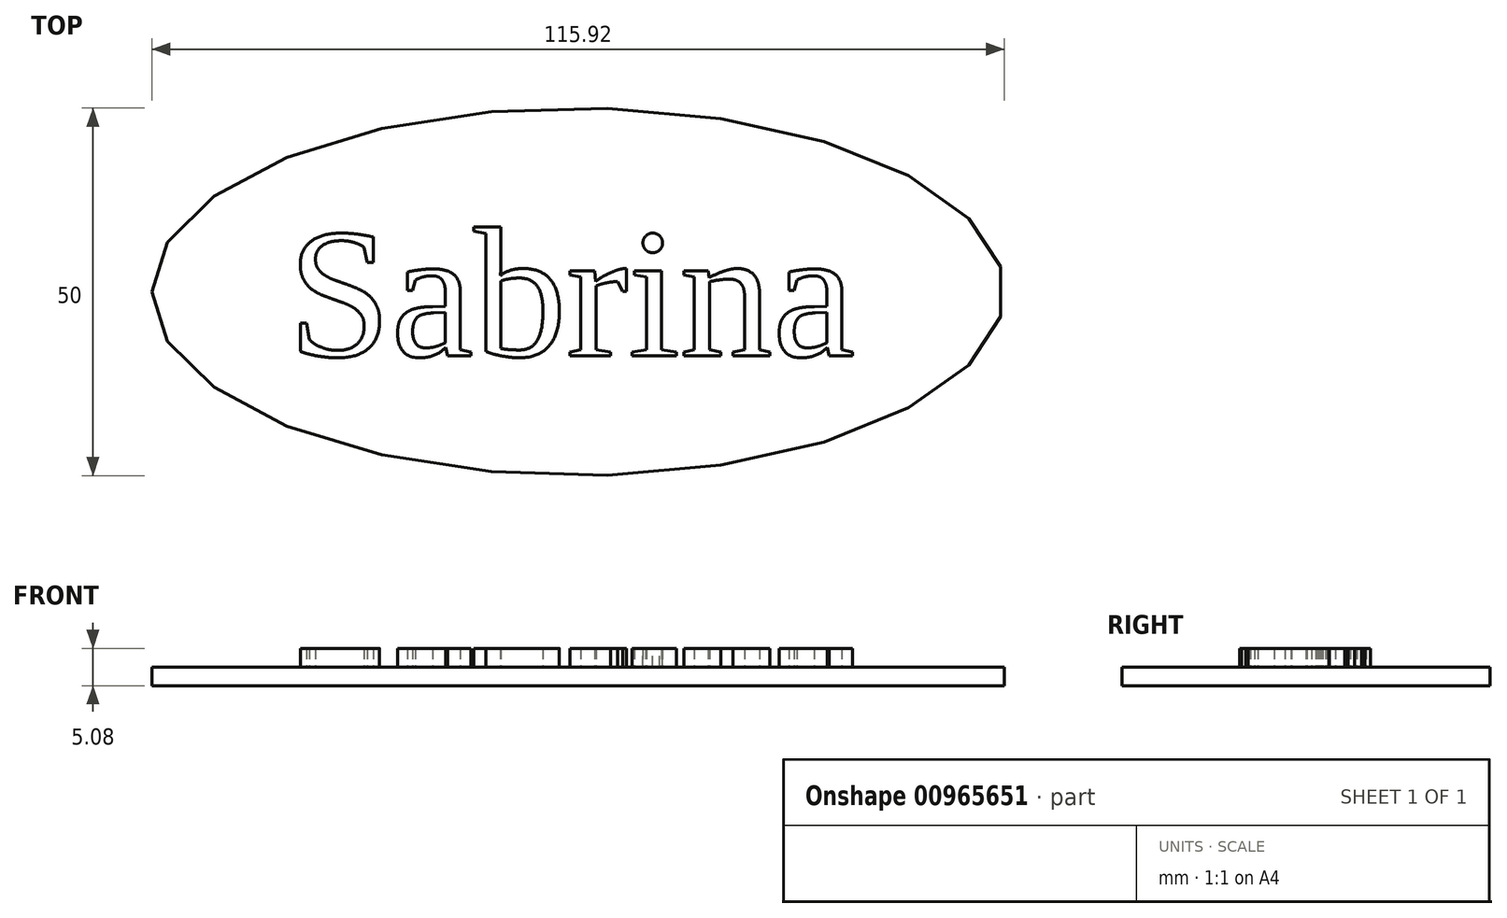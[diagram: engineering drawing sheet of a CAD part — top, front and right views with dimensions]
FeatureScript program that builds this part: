
annotation { "Feature Type Name" : "Feature", "Feature Type Description" : "" }
export const myFeature = defineFeature(function(context is Context, id is Id, definition is map)
    precondition{}
    {
        {
            var Q0;
            Q0=qCreatedBy(makeId("Top.planeOp"),FACE);
            var sketch = newSketch(context, id + "F0", { "sketchPlane" : qUnion([Q0])});
            skEllipse(sketch, "E0", {"center": v(0, 0) * mm, "majorRadius": 57.96 * mm, "minorRadius": 25 * mm, "majorAxis": v(-1, 0)});
            skSolve(sketch);
        }
        {
            var Q0;
            Q0=makeQuery(id+"F0.imprint","IMPRINT",FACE,{"disambiguationData":[TD([[makeQuery(id+"F0.imprint","IMPRINT",EDGE,{"derivedFrom":sQuery(id+"F0.wireOp",EDGE,"E0")}),1.0]])]});
            extrude(context, id + "F1", {"entities" : qUnion([Q0]), "depth" : 2.54 * mm, "offsetDistance" : 25.4 * mm});
        }
        {
            var Q0;
            Q0=makeQuery(id+"F1.opExtrude","CAP_FACE",FACE,{"disambiguationData":[OSD([sQuery(id+"F0.wireOp",EDGE,"E0")])],"isStart":false});
            var sketch = newSketch(context, id + "F2", { "sketchPlane" : qUnion([Q0])});
            skText(sketch, "E1", { "text": "Sabrina", "fontName": "Tinos-Regular.ttf"});
            const initialGuessF2  = {"E1": [-0.03946, -0.00873, 1, 0, 0.01818]};
            skSetInitialGuess(sketch, initialGuessF2);
            skSolve(sketch);
        }
        {
            var Q0;
            Q0 = qSketchRegion(id + "F2", true);
            extrude(context, id + "F3", {"entities" : qUnion([Q0]), "operationType" : NewBodyOperationType.ADD, "depth" : 2.54 * mm, "offsetDistance" : 25.4 * mm});
        }
    });
